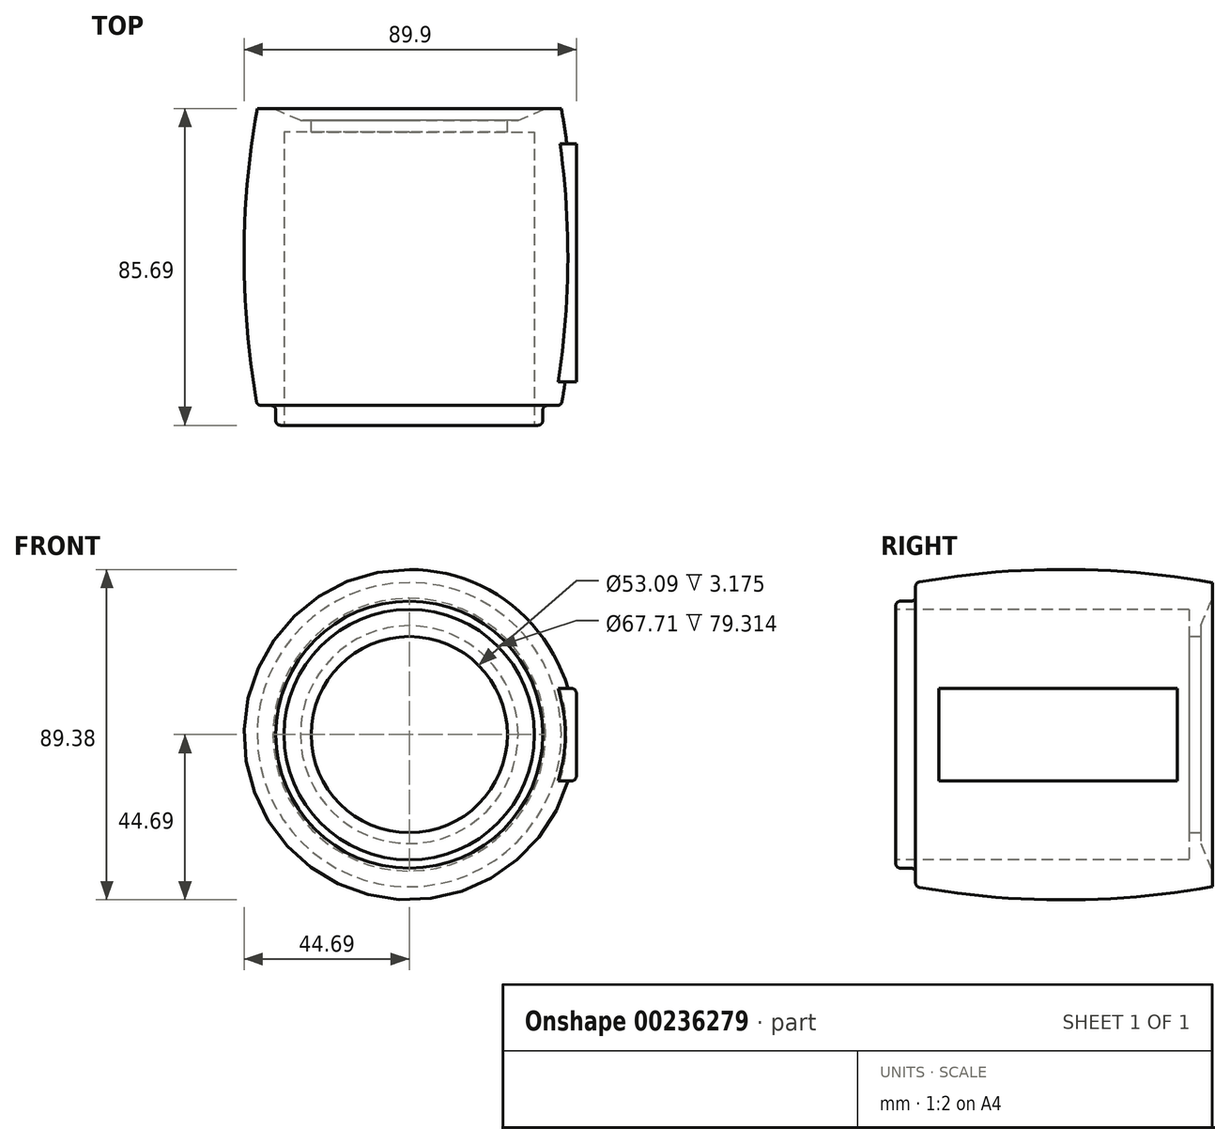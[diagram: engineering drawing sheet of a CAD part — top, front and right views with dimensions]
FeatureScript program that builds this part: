
annotation { "Feature Type Name" : "Feature", "Feature Type Description" : "" }
export const myFeature = defineFeature(function(context is Context, id is Id, definition is map)
    precondition{}
    {
        {
            var Q0;
            Q0=qCreatedBy(makeId("Right.planeOp"),FACE);
            var sketch = newSketch(context, id + "F0", { "sketchPlane" : qUnion([Q0])});
            skLineSegment(sketch, "E0", {"start": v(0, 0) * mm, "end": v(0, 26.54) * mm});
            skLineSegment(sketch, "E1", {"start": v(0, 26.54) * mm, "end": v(6.29, 26.54) * mm});
            skLineSegment(sketch, "E2", {"start": v(6.29, 26.54) * mm, "end": v(6.29, 29.46) * mm});
            skLineSegment(sketch, "E3", {"start": v(6.29, 29.46) * mm, "end": v(9.49, 36.86) * mm});
            skLineSegment(sketch, "E4", {"start": v(9.49, 36.86) * mm, "end": v(9.49, 41.14) * mm});
            skArc(sketch, "E5", {"start": v(9.49, 41.14) * mm, "mid": v(-30.68, 44.7) * mm, "end": v(-70.85, 41.14) * mm});
            skLineSegment(sketch, "E6", {"start": v(-70.85, 41.14) * mm, "end": v(-70.85, 36.12) * mm});
            skLineSegment(sketch, "E7", {"start": v(-70.85, 36.12) * mm, "end": v(-76.2, 36.12) * mm});
            skLineSegment(sketch, "E8", {"start": v(-76.2, 36.12) * mm, "end": v(-76.2, 0) * mm});
            skLineSegment(sketch, "E9", {"start": v(-76.2, 0) * mm, "end": v(0, 0) * mm});
            skSolve(sketch);
        }
        {
            var Q0;
            Q0=qCreatedBy(makeId("Right.planeOp"),FACE);
            var sketch = newSketch(context, id + "F1", { "sketchPlane" : qUnion([Q0])});
            skLineSegment(sketch, "E10", {"start": v(0, 0) * mm, "end": v(-188.15, 0) * mm});
            skSolve(sketch);
        }
        {
            var Q0;
            Q0=makeQuery(id+"F0.imprint","IMPRINT",FACE,{"disambiguationData":[TD([[makeQuery(id+"F0.imprint","IMPRINT",EDGE,{"derivedFrom":sQuery(id+"F0.wireOp",EDGE,"E0")}),1.0]])]});
            var Q1;
            Q1=sQuery(id+"F1.wireOp",EDGE,"E10");
            revolve(context, id + "F2", {"entities" : qUnion([Q0]), "axis" : qUnion([Q1]), "revolveType" : RevolveType.FULL});
        }
        {
            var Q0;
            Q0=makeQuery(id+"F2.opRevolve","SWEPT_FACE",FACE,{"disambiguationData":[OSD([sQuery(id+"F0.wireOp",EDGE,"E0")])]});
            var sketch = newSketch(context, id + "F3", { "sketchPlane" : qUnion([Q0])});
            skCircle(sketch, "E11.0", {"center": v(0, 0) * mm, "radius": 26.54 * mm});
            skSolve(sketch);
        }
        {
            var Q0;
            Q0=makeQuery(id+"F3.imprint","IMPRINT",FACE,{"disambiguationData":[TD([[makeQuery(id+"F3.imprint","IMPRINT",EDGE,{"derivedFrom":sQuery(id+"F3.wireOp",EDGE,"E11.0")}),1.0]])]});
            extrude(context, id + "F4", {"entities" : qUnion([Q0]), "operationType" : NewBodyOperationType.REMOVE, "oppositeDirection" : true, "depth" : 114.55 * mm});
        }
        {
            var Q0;
            Q0=makeQuery(id+"F2.opRevolve","SWEPT_FACE",FACE,{"disambiguationData":[OSD([sQuery(id+"F0.wireOp",EDGE,"E2")])]});
            cPlane(context, id + "F5", {"entities" : qUnion([Q0]), "cplaneType" : CPlaneType.OFFSET, "offset" : 3.17 * mm, "oppositeDirection" : true, "width" : 152.4 * mm, "height" : 152.4 * mm});
        }
        {
            var Q0;
            Q0=qCreatedBy(id+"F5.planeOp",FACE);
            var sketch = newSketch(context, id + "F6", { "sketchPlane" : qUnion([Q0])});
            skCircle(sketch, "E12", {"center": v(0, 0) * mm, "radius": 28.54 * mm});
            skSolve(sketch);
        }
        {
            var Q0;
            Q0=makeQuery(id+"F6.imprint","IMPRINT",FACE,{"disambiguationData":[TD([[makeQuery(id+"F6.imprint","IMPRINT",EDGE,{"derivedFrom":sQuery(id+"F6.wireOp",EDGE,"E12")}),1.0]])]});
            extrude(context, id + "F7", {"entities" : qUnion([Q0]), "operationType" : NewBodyOperationType.REMOVE, "endBound" : BoundingType.THROUGH_ALL, "oppositeDirection" : true, "depth" : 25.4 * mm});
        }
        {
            var Q0;
            Q0=makeQuery(id+"F2.opRevolve","SWEPT_FACE",FACE,{"disambiguationData":[OSD([sQuery(id+"F0.wireOp",EDGE,"E8")])]});
            var sketch = newSketch(context, id + "F8", { "sketchPlane" : qUnion([Q0])});
            skCircle(sketch, "E13", {"center": v(0, 0) * mm, "radius": 43.03 * mm});
            skSolve(sketch);
        }
        {
            var Q0;
            Q0=makeQuery(id+"F8.imprint","IMPRINT",FACE,{"disambiguationData":[TD([[makeQuery(id+"F8.imprint","IMPRINT",EDGE,{"derivedFrom":makeQuery(id+"F7.boolean.opBoolean","INTERSECT",EDGE,{"derivedFrom":[makeQuery(id+"F2.opRevolve","SWEPT_FACE",FACE,{"disambiguationData":[OSD([sQuery(id+"F0.wireOp",EDGE,"E8")])]}),makeQuery(id+"F7.opExtrude","SWEPT_FACE",FACE,{"disambiguationData":[OSD([sQuery(id+"F6.wireOp",EDGE,"E12")])]})]})}),1.0]])]});
            var sketch = newSketch(context, id + "F9", { "sketchPlane" : qUnion([Q0])});
            skCircle(sketch, "E14", {"center": v(0, 0) * mm, "radius": 33.86 * mm});
            skSolve(sketch);
        }
        {
            var Q0;
            Q0=makeQuery(id+"F9.imprint","IMPRINT",FACE,{"disambiguationData":[TD([[makeQuery(id+"F9.imprint","IMPRINT",EDGE,{"derivedFrom":sQuery(id+"F9.wireOp",EDGE,"E14")}),1.0]])]});
            var Q1;
            Q1=makeQuery(id+"F7.boolean.opBoolean","COPY",FACE,{"derivedFrom":makeQuery(id+"F7.opExtrude","CAP_FACE",FACE,{"disambiguationData":[OSD([sQuery(id+"F6.wireOp",EDGE,"E12")])],"isStart":true})});
            extrude(context, id + "F10", {"entities" : qUnion([Q0]), "operationType" : NewBodyOperationType.REMOVE, "endBound" : BoundingType.UP_TO_SURFACE, "oppositeDirection" : true, "endBoundEntityFace" : qUnion([Q1]), "depth" : 25.4 * mm});
        }
        {
            var Q0;
            Q0=qCreatedBy(makeId("Right.planeOp"),FACE);
            cPlane(context, id + "F11", {"entities" : qUnion([Q0]), "cplaneType" : CPlaneType.OFFSET, "offset" : 45.2 * mm, "width" : 152.4 * mm, "height" : 152.4 * mm});
        }
        {
            var Q0;
            Q0=qCreatedBy(id+"F11.planeOp",FACE);
            var sketch = newSketch(context, id + "F12", { "sketchPlane" : qUnion([Q0])});
            skLineSegment(sketch, "E15", {"start": v(0, 0) * mm, "end": v(0, 12.49) * mm});
            skLineSegment(sketch, "E16", {"start": v(0, 12.49) * mm, "end": v(-64.5, 12.49) * mm});
            skLineSegment(sketch, "E17.MirrorCS", {"start": v(0, -12.49) * mm, "end": v(-64.5, -12.49) * mm});
            skLineSegment(sketch, "E18.MirrorCS", {"start": v(0, 0) * mm, "end": v(0, -12.49) * mm});
            skLineSegment(sketch, "E19.0", {"start": v(-64.5, 12.49) * mm, "end": v(-64.5, -12.49) * mm});
            skPoint(sketch, "E20.0.start.orphan", {"position": v(-70.85, 41.14) * mm});
            skPoint(sketch, "E21.start.orphan", {"position": v(-85.09, 0) * mm});
            skPoint(sketch, "E22.MirrorCS.end.orphan", {"position": v(-85.09, -12.49) * mm});
            skPoint(sketch, "E23.orphan", {"position": v(-85.09, 12.49) * mm});
            skPoint(sketch, "E24.trimOffspring.end.orphan", {"position": v(-70.85, -41.14) * mm});
            skSolve(sketch);
        }
        {
            var Q0;
            Q0=makeQuery(id+"F12.imprint","IMPRINT",FACE,{"disambiguationData":[TD([[makeQuery(id+"F12.imprint","IMPRINT",EDGE,{"derivedFrom":sQuery(id+"F12.wireOp",EDGE,"E15")}),1.0]])]});
            extrude(context, id + "F13", {"entities" : qUnion([Q0]), "operationType" : NewBodyOperationType.ADD, "endBound" : BoundingType.UP_TO_NEXT, "oppositeDirection" : true, "depth" : 25.4 * mm});
        }
        {
            var Q0;
            Q0=makeQuery(id+"F2.opRevolve","SWEPT_EDGE",EDGE,{"disambiguationData":[OSD([sQuery(id+"F0.wireOp",EDGE,"E7"),sQuery(id+"F0.wireOp",EDGE,"E8")])]});
            var Q1;
            Q1=makeQuery(id+"F2.opRevolve","SWEPT_EDGE",EDGE,{"disambiguationData":[OSD([sQuery(id+"F0.wireOp",EDGE,"E6"),sQuery(id+"F0.wireOp",EDGE,"E7")])]});
            var Q2;
            Q2=makeQuery(id+"F2.opRevolve","SWEPT_EDGE",EDGE,{"disambiguationData":[OSD([sQuery(id+"F0.wireOp",EDGE,"E5"),sQuery(id+"F0.wireOp",EDGE,"E6")])]});
            var Q3;
            Q3=makeQuery(id+"F13.opExtrude","TWEAK_EDGE",EDGE,{"derivedFrom":[makeQuery(id+"F2.opRevolve","SWEPT_FACE",FACE,{"disambiguationData":[OSD([sQuery(id+"F0.wireOp",EDGE,"E5")])]}),makeQuery(id+"F12.imprint","IMPRINT",EDGE,{"derivedFrom":sQuery(id+"F12.wireOp",EDGE,"E16")})]});
            var Q4;
            Q4=makeQuery(id+"F13.opExtrude","CAP_EDGE",EDGE,{"disambiguationData":[OSD([sQuery(id+"F12.wireOp",EDGE,"E16")])],"isStart":true});
            var Q5;
            Q5=makeQuery(id+"F13.opExtrude","CAP_EDGE",EDGE,{"disambiguationData":[OSD([sQuery(id+"F12.wireOp",EDGE,"E17.MirrorCS")])],"isStart":true});
            var Q6;
            Q6=makeQuery(id+"F13.opExtrude","TWEAK_EDGE",EDGE,{"derivedFrom":[makeQuery(id+"F2.opRevolve","SWEPT_FACE",FACE,{"disambiguationData":[OSD([sQuery(id+"F0.wireOp",EDGE,"E5")])]}),makeQuery(id+"F12.imprint","IMPRINT",EDGE,{"derivedFrom":sQuery(id+"F12.wireOp",EDGE,"E17.MirrorCS")})]});
            fillet(context, id + "F14", {"entities" : qUnion([Q0, Q1, Q2, Q3, Q4, Q5, Q6]), "radius" : 1.27 * mm, "tangentPropagation" : true, "allowEdgeOverflow" : false});
        }
    });
